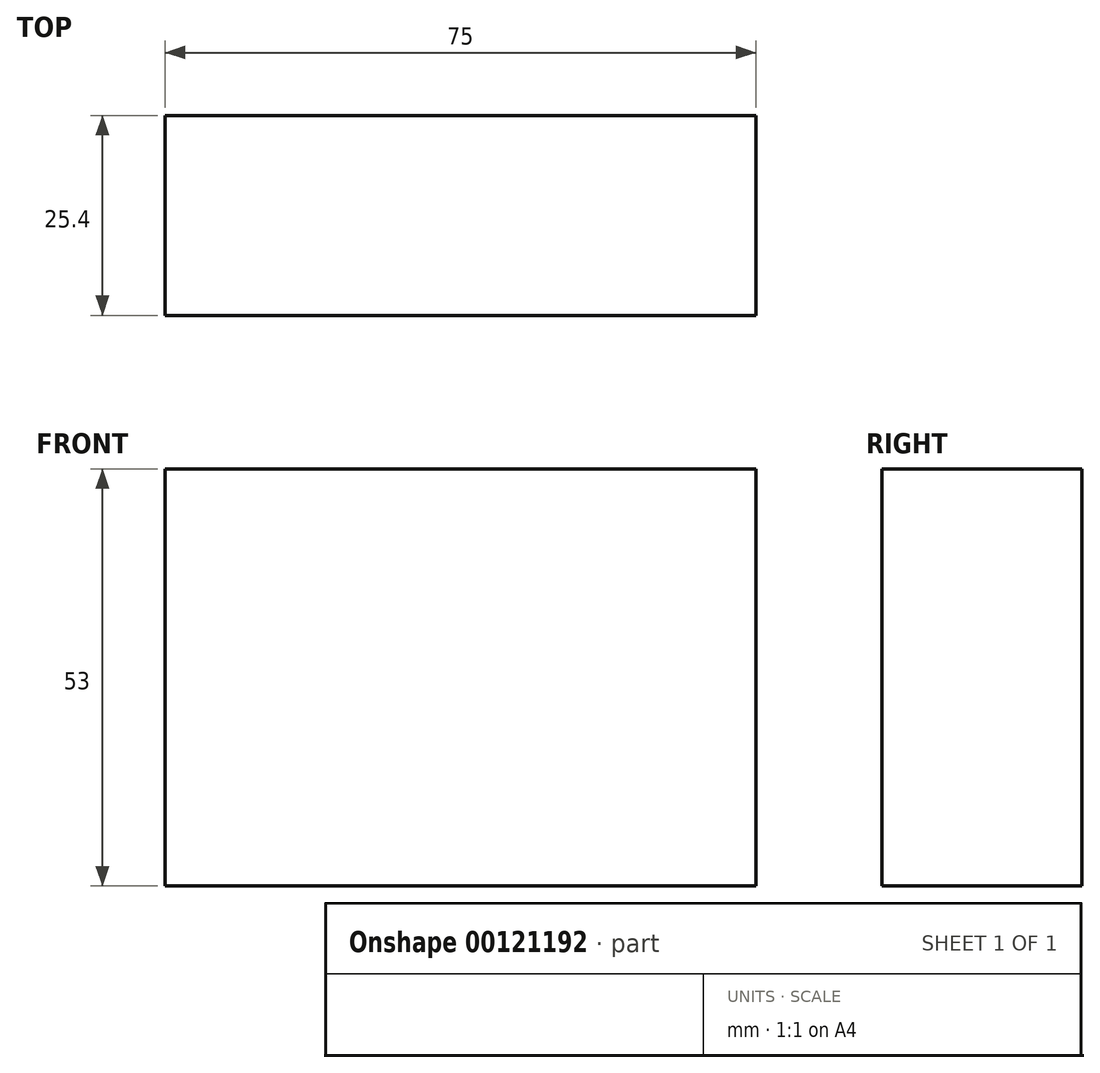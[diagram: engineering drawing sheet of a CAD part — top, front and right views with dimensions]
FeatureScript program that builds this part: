
annotation { "Feature Type Name" : "Feature", "Feature Type Description" : "" }
export const myFeature = defineFeature(function(context is Context, id is Id, definition is map)
    precondition{}
    {
        {
            var Q0;
            Q0=qCreatedBy(makeId("Front.planeOp"),FACE);
            var sketch = newSketch(context, id + "F0", { "sketchPlane" : qUnion([Q0])});
            skLineSegment(sketch, "E0.bottom", {"start": v(37.5, -26.5) * mm, "end": v(-37.5, -26.5) * mm});
            skLineSegment(sketch, "E0.top", {"start": v(37.5, 26.5) * mm, "end": v(-37.5, 26.5) * mm});
            skLineSegment(sketch, "E0.left", {"start": v(37.5, -26.5) * mm, "end": v(37.5, 26.5) * mm});
            skLineSegment(sketch, "E0.right", {"start": v(-37.5, -26.5) * mm, "end": v(-37.5, 26.5) * mm});
            skPoint(sketch, "E0.middle", {"position": v(0, 0) * mm});
            skSolve(sketch);
        }
        {
            var Q0;
            Q0 = qSketchRegion(id + "F0", true);
            extrude(context, id + "F1", {"entities" : qUnion([Q0]), "depth" : 25.4 * mm});
        }
    });
